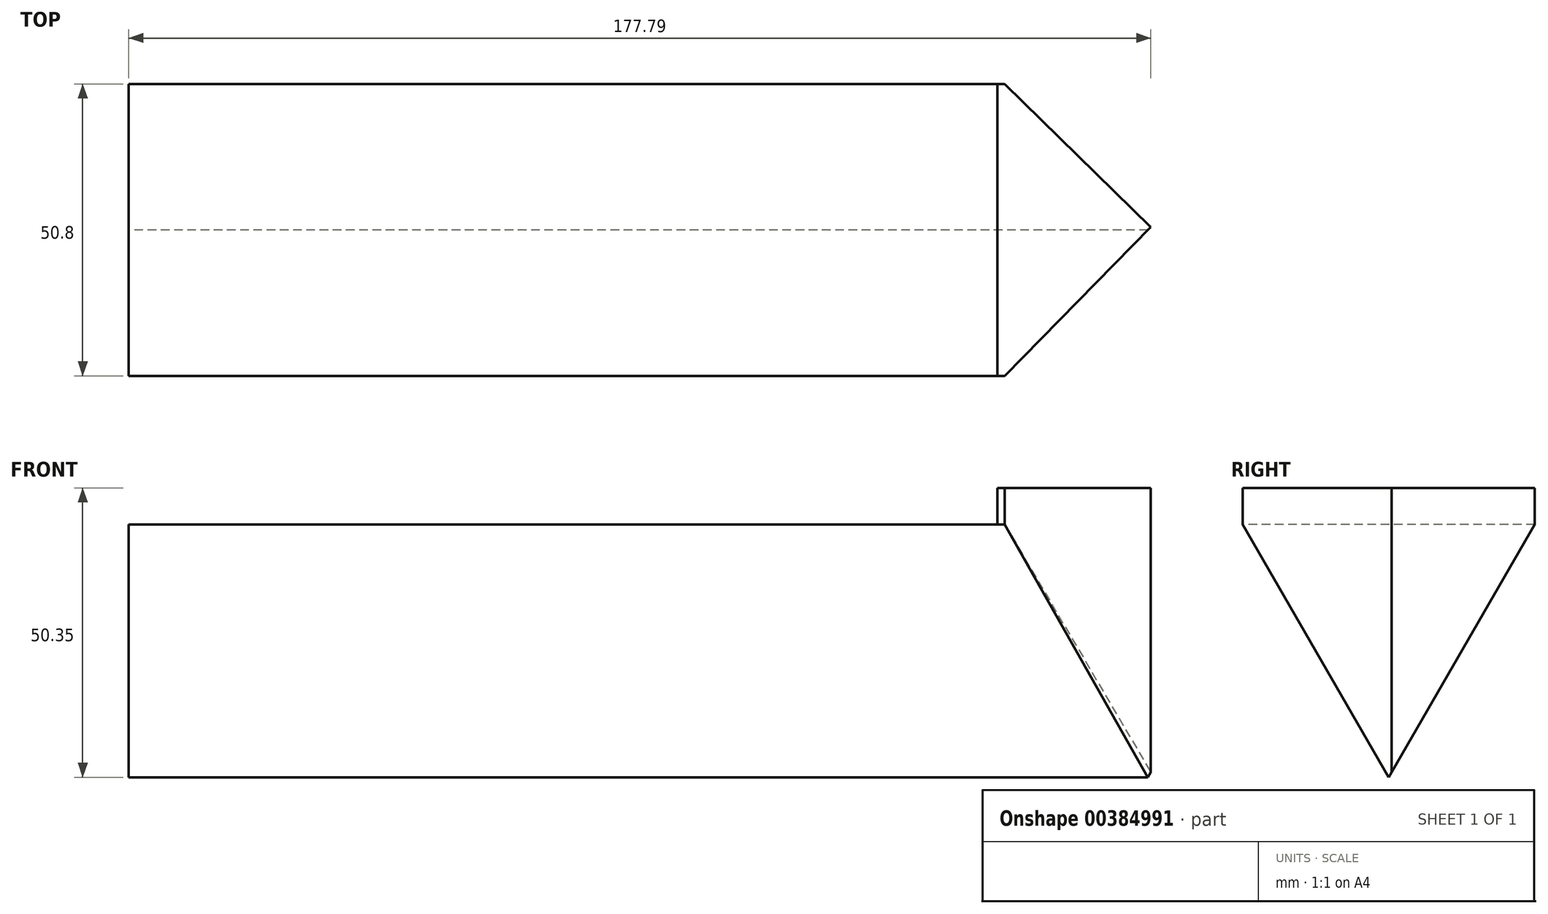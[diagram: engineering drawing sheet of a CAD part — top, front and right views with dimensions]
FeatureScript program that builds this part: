
annotation { "Feature Type Name" : "Feature", "Feature Type Description" : "" }
export const myFeature = defineFeature(function(context is Context, id is Id, definition is map)
    precondition{}
    {
        {
            var Q0;
            Q0=qCreatedBy(makeId("Right.planeOp"),FACE);
            var sketch = newSketch(context, id + "F0", { "sketchPlane" : qUnion([Q0])});
            skCircle(sketch, "E0.cCircle", {"center": v(-56.23, 15.55) * mm, "radius": 14.66 * mm, "construction": true});
            skLineSegment(sketch, "E0.0", {"start": v(-81.63, 30.22) * mm, "end": v(-30.83, 30.22) * mm});
            skLineSegment(sketch, "E0.1", {"start": v(-30.83, 30.22) * mm, "end": v(-56.23, -13.78) * mm});
            skLineSegment(sketch, "E0.2", {"start": v(-56.23, -13.78) * mm, "end": v(-81.63, 30.22) * mm});
            skPoint(sketch, "E0.0.midPoint", {"position": v(-56.23, 30.22) * mm});
            skPoint(sketch, "E1.0.midPoint", {"position": v(30.1, 22.9) * mm});
            skPoint(sketch, "E2.orphan", {"position": v(42.82, 45.79) * mm});
            skPoint(sketch, "E1.cCircle.center.orphan", {"position": v(43.3, 15.55) * mm});
            skPoint(sketch, "E1.2.end.orphan", {"position": v(17.37, 0.02) * mm});
            skSolve(sketch);
        }
        {
            var Q0;
            Q0=makeQuery(id+"F0.imprint","IMPRINT",FACE,{"disambiguationData":[TD([[makeQuery(id+"F0.imprint","IMPRINT",EDGE,{"derivedFrom":sQuery(id+"F0.wireOp",EDGE,"E0.0")}),-1.0]])]});
            extrude(context, id + "F1", {"entities" : qUnion([Q0]), "depth" : 152.4 * mm, "offsetDistance" : 25.4 * mm});
        }
        {
            var Q0;
            Q0=makeQuery(id+"F1.opExtrude","SWEPT_FACE",FACE,{"disambiguationData":[OSD([sQuery(id+"F0.wireOp",EDGE,"E0.0")])]});
            var sketch = newSketch(context, id + "F2", { "sketchPlane" : qUnion([Q0])});
            skLineSegment(sketch, "E3", {"start": v(152.4, -30.83) * mm, "end": v(177.8, -55.72) * mm});
            skLineSegment(sketch, "E4", {"start": v(177.8, -55.72) * mm, "end": v(152.4, -81.63) * mm});
            skSolve(sketch);
        }
        {
            var Q0;
            Q0=makeQuery(id+"F2.imprint","IMPRINT",FACE,{"disambiguationData":[TD([[makeQuery(id+"F2.imprint","IMPRINT",EDGE,{"derivedFrom":sQuery(id+"F2.wireOp",EDGE,"E3")}),-1.0]])]});
            extrude(context, id + "F3", {"entities" : qUnion([Q0]), "operationType" : NewBodyOperationType.ADD, "oppositeDirection" : true, "depth" : 44.45 * mm, "offsetDistance" : 25.4 * mm});
        }
        {
            var Q0;
            Q0=makeQuery(id+"F3.opExtrude","SWEPT_FACE",FACE,{"disambiguationData":[OSD([sQuery(id+"F0.wireOp",EDGE,"E0.0")])]});
            var sketch = newSketch(context, id + "F4", { "sketchPlane" : qUnion([Q0])});
            skLineSegment(sketch, "E5", {"start": v(30.83, 30.22) * mm, "end": v(56.23, -13.78) * mm});
            skLineSegment(sketch, "E6", {"start": v(30.83, -14.23) * mm, "end": v(30.83, 30.22) * mm});
            skLineSegment(sketch, "E7", {"start": v(81.63, -14.23) * mm, "end": v(81.63, 30.22) * mm});
            skLineSegment(sketch, "E8", {"start": v(81.63, 30.22) * mm, "end": v(56.23, -13.78) * mm});
            skLineSegment(sketch, "E9", {"start": v(30.83, -14.23) * mm, "end": v(56.23, -14.23) * mm});
            skLineSegment(sketch, "E10", {"start": v(56.23, -14.23) * mm, "end": v(81.63, -14.23) * mm});
            skSolve(sketch);
        }
        {
            var Q0;
            Q0 = qSketchRegion(id + "F4", true);
            extrude(context, id + "F5", {"entities" : qUnion([Q0]), "operationType" : NewBodyOperationType.REMOVE, "oppositeDirection" : true, "depth" : 25.4 * mm, "offsetDistance" : 25.4 * mm});
        }
        {
            var Q0;
            {var subQ0=sQuery(id+"F0.wireOp",EDGE,"E0.0");Q0=makeQuery(id+"F3.boolean.opBoolean","MERGE",FACE,{"derivedFrom":[makeQuery(id+"F1.opExtrude","SWEPT_FACE",FACE,{"disambiguationData":[OSD([subQ0])]}),makeQuery(id+"F3.opExtrude","CAP_FACE",FACE,{"disambiguationData":[OSD([subQ0,sQuery(id+"F2.wireOp",EDGE,"E3"),sQuery(id+"F2.wireOp",EDGE,"E4")])],"isStart":true})]});}
            var sketch = newSketch(context, id + "F6", { "sketchPlane" : qUnion([Q0])});
            skLineSegment(sketch, "E11", {"start": v(152.4, -30.83) * mm, "end": v(152.4, -81.63) * mm});
            skLineSegment(sketch, "E12", {"start": v(152.4, -81.63) * mm, "end": v(177.8, -55.72) * mm});
            skLineSegment(sketch, "E13", {"start": v(177.8, -55.72) * mm, "end": v(152.4, -30.83) * mm});
            skSolve(sketch);
        }
        {
            var Q0;
            Q0=makeQuery(id+"F6.imprint","IMPRINT",FACE,{"disambiguationData":[TD([[makeQuery(id+"F6.imprint","IMPRINT",EDGE,{"derivedFrom":sQuery(id+"F6.wireOp",EDGE,"E11")}),1.0]])]});
            extrude(context, id + "F7", {"entities" : qUnion([Q0]), "operationType" : NewBodyOperationType.ADD, "depth" : 5.08 * mm, "offsetDistance" : 25.4 * mm});
        }
        {
            var Q0;
            Q0=makeQuery(id+"F7.opExtrude","SWEPT_FACE",FACE,{"disambiguationData":[OSD([sQuery(id+"F6.wireOp",EDGE,"E11")])]});
            extrude(context, id + "F8", {"entities" : qUnion([Q0]), "operationType" : NewBodyOperationType.ADD, "depth" : 1.27 * mm, "offsetDistance" : 25.4 * mm});
        }
        {
            var Q0;
            {var subQ0=sQuery(id+"F6.wireOp",EDGE,"E11");Q0=makeQuery(id+"F8.boolean.opBoolean","MERGE",FACE,{"derivedFrom":[makeQuery(id+"F7.opExtrude","CAP_FACE",FACE,{"disambiguationData":[OSD([subQ0,sQuery(id+"F6.wireOp",EDGE,"E12"),sQuery(id+"F6.wireOp",EDGE,"E13")])],"isStart":false}),makeQuery(id+"F8.opExtrude","SWEPT_FACE",FACE,{"disambiguationData":[OSD([subQ0]),TDD([makeQuery(id+"F7.opExtrude","CAP_EDGE",EDGE,{"disambiguationData":[OSD([subQ0])],"isStart":false})])]})]});}
            extrude(context, id + "F9", {"entities" : qUnion([Q0]), "operationType" : NewBodyOperationType.ADD, "depth" : 1.27 * mm, "offsetDistance" : 25.4 * mm});
        }
    });
